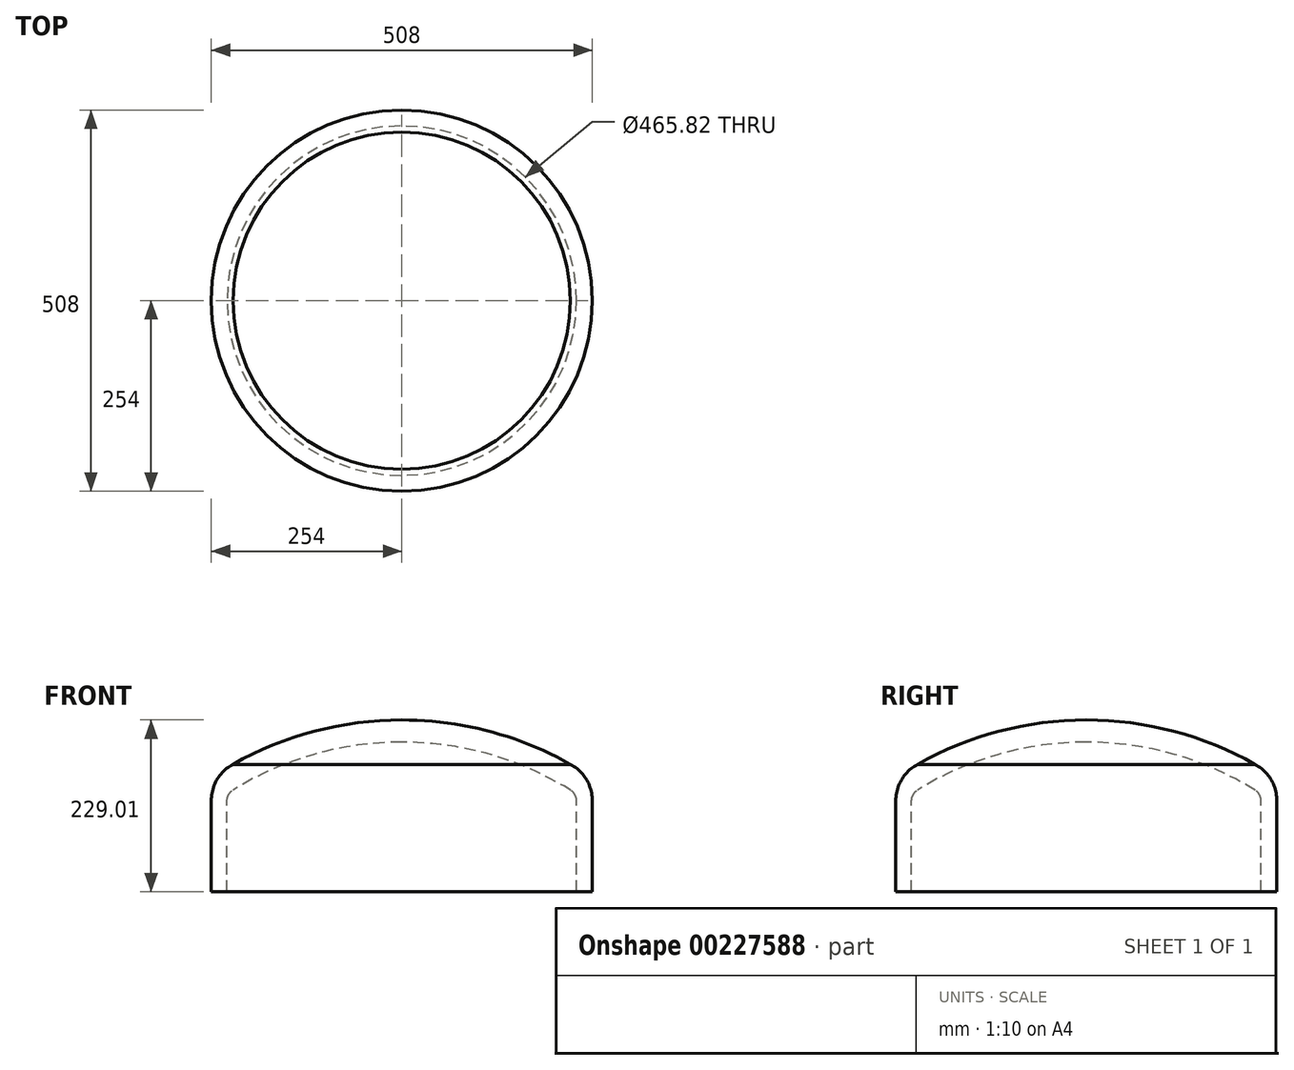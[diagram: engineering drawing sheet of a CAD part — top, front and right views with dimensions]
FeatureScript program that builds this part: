
annotation { "Feature Type Name" : "Feature", "Feature Type Description" : "" }
export const myFeature = defineFeature(function(context is Context, id is Id, definition is map)
    precondition{}
    {
        {
            var Q0;
            Q0=qCreatedBy(makeId("Front.planeOp"),FACE);
            var sketch = newSketch(context, id + "F0", { "sketchPlane" : qUnion([Q0])});
            skArc(sketch, "E0.MirrorCS", {"start": v(-254, 0) * mm, "mid": v(-246.17, 28.26) * mm, "end": v(-224.9, 48.46) * mm});
            skArc(sketch, "E1.MirrorCS", {"start": v(-232.9, 0) * mm, "mid": v(-230.82, 8.03) * mm, "end": v(-225.1, 14.03) * mm});
            skPoint(sketch, "E2.orphan", {"position": v(-144.2, 0) * mm});
            skArc(sketch, "E3", {"start": v(0, 78.06) * mm, "mid": v(-117.01, 61.74) * mm, "end": v(-225.1, 14.03) * mm});
            skLineSegment(sketch, "E4", {"start": v(-254, 0) * mm, "end": v(-254, -121.4) * mm});
            skLineSegment(sketch, "E5", {"start": v(-232.9, 0) * mm, "end": v(-232.9, -121.41) * mm});
            skLineSegment(sketch, "E6", {"start": v(-254, -121.4) * mm, "end": v(-232.9, -121.41) * mm});
            skLineSegment(sketch, "E7", {"start": v(0, 107.6) * mm, "end": v(0, -122.42) * mm});
            skPoint(sketch, "E7.endSnap0", {"position": v(0, 107.6) * mm});
            skArc(sketch, "E8.trimOffspring", {"start": v(0, 107.6) * mm, "mid": v(-117.78, 92.17) * mm, "end": v(-227.61, 46.92) * mm});
            skSolve(sketch);
        }
        {
            var Q0;
            Q0 = qSketchRegion(id + "F0", true);
            var Q1;
            Q1=sQuery(id+"F0.wireOp",EDGE,"E7");
            revolve(context, id + "F1", {"entities" : qUnion([Q0]), "axis" : qUnion([Q1]), "revolveType" : RevolveType.FULL});
        }
    });
